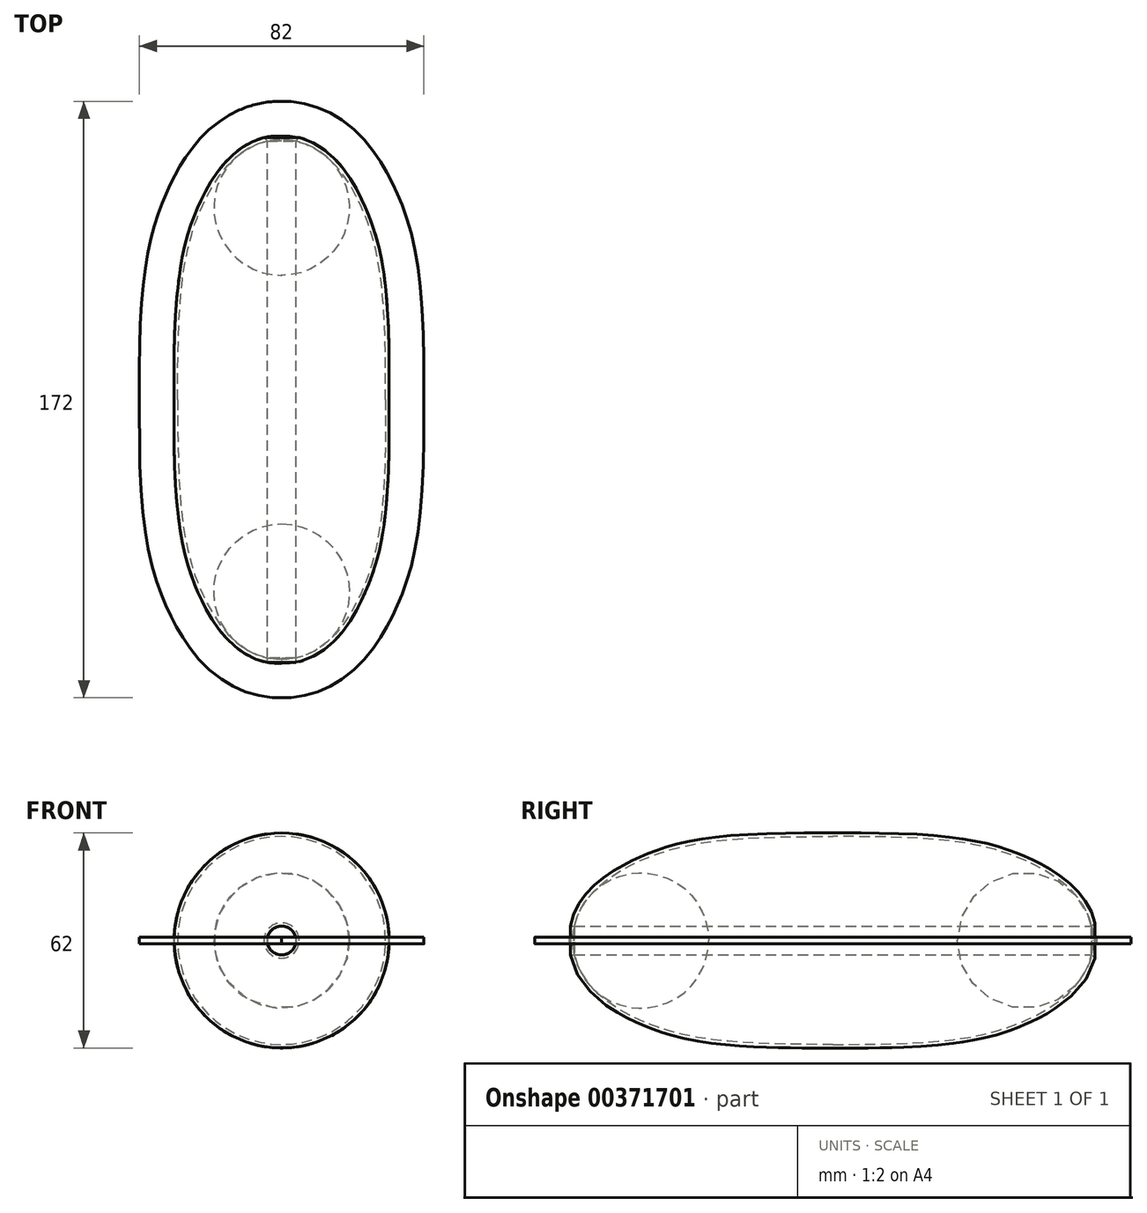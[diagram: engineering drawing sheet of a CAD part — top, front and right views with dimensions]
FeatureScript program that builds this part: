
annotation { "Feature Type Name" : "Feature", "Feature Type Description" : "" }
export const myFeature = defineFeature(function(context is Context, id is Id, definition is map)
    precondition{}
    {
        {
            var Q0;
            Q0=qCreatedBy(makeId("Top.planeOp"),FACE);
            var sketch = newSketch(context, id + "F0", { "sketchPlane" : qUnion([Q0])});
            skLineSegment(sketch, "E0", {"start": v(-51.66, 84.82) * mm, "end": v(-51.66, -137.93) * mm});
            skFitSpline(sketch, "E1", {"points": [v(-51.66, 75) * mm, v(-74.62, 55.7) * mm, v(-81.66, 0) * mm], "startDerivative": vector(-82.27, 0) * mm, "endDerivative": vector(0, -150.55) * mm});
            skFitSpline(sketch, "E2.MirrorCS", {"points": [v(-51.66, -75) * mm, v(-74.62, -55.7) * mm, v(-81.66, 0) * mm], "startDerivative": vector(-82.27, 0) * mm, "endDerivative": vector(0, 150.55) * mm});
            skFitSpline(sketch, "E3.MirrorCS", {"points": [v(-51.66, 75) * mm, v(-28.7, 55.7) * mm, v(-21.66, 0) * mm], "startDerivative": vector(82.27, 0) * mm, "endDerivative": vector(0, -150.55) * mm});
            skFitSpline(sketch, "E4.MirrorCS", {"points": [v(-51.66, -75) * mm, v(-28.7, -55.7) * mm, v(-21.66, 0) * mm], "startDerivative": vector(82.27, 0) * mm, "endDerivative": vector(0, 150.55) * mm});
            skLineSegment(sketch, "E5", {"start": v(-55.82, -80.1) * mm, "end": v(-55.82, 74.56) * mm});
            skLineSegment(sketch, "E6", {"start": v(-55.82, 74.56) * mm, "end": v(-64.04, 83.73) * mm});
            skFitSpline(sketch, "E7.0", {"points": [v(-51.66, 76) * mm, v(-53.46, 76) * mm, v(-56.85, 75.56) * mm, v(-61.36, 73.76) * mm, v(-65.28, 71.04) * mm, v(-68.66, 67.6) * mm, v(-71.55, 63.68) * mm, v(-73.59, 60.14) * mm, v(-75.03, 57.23) * mm, v(-76.01, 55.05) * mm, v(-76.91, 52.86) * mm, v(-78, 49.9) * mm, v(-79.17, 46.1) * mm, v(-80.29, 41.26) * mm, v(-81.15, 36.05) * mm, v(-82, 28.44) * mm, v(-82.56, 17.39) * mm, v(-82.66, 6.28) * mm, v(-82.66, 0) * mm]});
            skFitSpline(sketch, "E7.1", {"points": [v(-51.66, 76) * mm, v(-49.86, 76) * mm, v(-46.47, 75.56) * mm, v(-41.96, 73.76) * mm, v(-38.04, 71.04) * mm, v(-34.66, 67.6) * mm, v(-31.77, 63.68) * mm, v(-29.73, 60.14) * mm, v(-28.3, 57.23) * mm, v(-27.3, 55.05) * mm, v(-26.4, 52.86) * mm, v(-25.32, 49.9) * mm, v(-24.15, 46.1) * mm, v(-23.03, 41.26) * mm, v(-22.17, 36.05) * mm, v(-21.33, 28.44) * mm, v(-20.76, 17.39) * mm, v(-20.66, 6.28) * mm, v(-20.66, 0) * mm]});
            skFitSpline(sketch, "E7.2", {"points": [v(-51.66, -76) * mm, v(-49.86, -76) * mm, v(-46.47, -75.56) * mm, v(-41.96, -73.76) * mm, v(-38.04, -71.04) * mm, v(-34.66, -67.6) * mm, v(-31.77, -63.68) * mm, v(-29.73, -60.14) * mm, v(-28.3, -57.23) * mm, v(-27.3, -55.05) * mm, v(-26.4, -52.86) * mm, v(-25.32, -49.9) * mm, v(-24.15, -46.1) * mm, v(-23.03, -41.26) * mm, v(-22.17, -36.05) * mm, v(-21.33, -28.44) * mm, v(-20.76, -17.39) * mm, v(-20.66, -6.28) * mm, v(-20.66, 0) * mm]});
            skFitSpline(sketch, "E7.3", {"points": [v(-51.66, -76) * mm, v(-53.46, -76) * mm, v(-56.85, -75.56) * mm, v(-61.36, -73.76) * mm, v(-65.28, -71.04) * mm, v(-68.66, -67.6) * mm, v(-71.55, -63.68) * mm, v(-73.59, -60.14) * mm, v(-75.03, -57.23) * mm, v(-76.01, -55.05) * mm, v(-76.91, -52.86) * mm, v(-78, -49.9) * mm, v(-79.17, -46.1) * mm, v(-80.29, -41.26) * mm, v(-81.15, -36.05) * mm, v(-82, -28.44) * mm, v(-82.56, -17.39) * mm, v(-82.66, -6.28) * mm, v(-82.66, 0) * mm]});
            skFitSpline(sketch, "E8.0", {"points": [v(-51.66, 86) * mm, v(-52.97, 86) * mm, v(-55.55, 85.84) * mm, v(-59.28, 85.13) * mm, v(-62.79, 83.98) * mm, v(-66.04, 82.47) * mm, v(-69, 80.65) * mm, v(-72.57, 77.91) * mm, v(-75.6, 74.83) * mm, v(-78.16, 71.59) * mm, v(-79.88, 69.1) * mm, v(-81.43, 66.57) * mm, v(-82.82, 64.03) * mm, v(-84.07, 61.5) * mm, v(-85.2, 59) * mm, v(-86.23, 56.49) * mm, v(-87.5, 53.07) * mm, v(-88.84, 48.68) * mm, v(-90.1, 43.18) * mm, v(-91.06, 37.38) * mm, v(-91.97, 29.15) * mm, v(-92.56, 17.6) * mm, v(-92.66, 6.33) * mm, v(-92.66, 0) * mm]});
            skFitSpline(sketch, "E8.1", {"points": [v(-51.66, 86) * mm, v(-50.35, 86) * mm, v(-47.77, 85.84) * mm, v(-44.04, 85.13) * mm, v(-40.53, 83.98) * mm, v(-37.28, 82.47) * mm, v(-34.31, 80.65) * mm, v(-30.75, 77.91) * mm, v(-27.73, 74.83) * mm, v(-25.16, 71.59) * mm, v(-23.44, 69.1) * mm, v(-21.89, 66.57) * mm, v(-20.5, 64.03) * mm, v(-19.25, 61.5) * mm, v(-18.12, 59) * mm, v(-17.09, 56.49) * mm, v(-15.83, 53.07) * mm, v(-14.48, 48.68) * mm, v(-13.21, 43.18) * mm, v(-12.26, 37.38) * mm, v(-11.35, 29.15) * mm, v(-10.76, 17.6) * mm, v(-10.66, 6.33) * mm, v(-10.66, 0) * mm]});
            skFitSpline(sketch, "E8.2", {"points": [v(-51.66, -86) * mm, v(-50.35, -86) * mm, v(-47.77, -85.84) * mm, v(-44.04, -85.13) * mm, v(-40.53, -83.98) * mm, v(-37.28, -82.47) * mm, v(-34.31, -80.65) * mm, v(-30.75, -77.91) * mm, v(-27.73, -74.83) * mm, v(-25.16, -71.59) * mm, v(-23.44, -69.1) * mm, v(-21.89, -66.57) * mm, v(-20.5, -64.03) * mm, v(-19.25, -61.5) * mm, v(-18.12, -59) * mm, v(-17.09, -56.49) * mm, v(-15.83, -53.07) * mm, v(-14.48, -48.68) * mm, v(-13.21, -43.18) * mm, v(-12.26, -37.38) * mm, v(-11.35, -29.15) * mm, v(-10.76, -17.6) * mm, v(-10.66, -6.33) * mm, v(-10.66, 0) * mm]});
            skFitSpline(sketch, "E8.3", {"points": [v(-51.66, -86) * mm, v(-52.97, -86) * mm, v(-55.55, -85.84) * mm, v(-59.28, -85.13) * mm, v(-62.79, -83.98) * mm, v(-66.04, -82.47) * mm, v(-69, -80.65) * mm, v(-72.57, -77.91) * mm, v(-75.6, -74.83) * mm, v(-78.16, -71.59) * mm, v(-79.88, -69.1) * mm, v(-81.43, -66.57) * mm, v(-82.82, -64.03) * mm, v(-84.07, -61.5) * mm, v(-85.2, -59) * mm, v(-86.23, -56.49) * mm, v(-87.5, -53.07) * mm, v(-88.84, -48.68) * mm, v(-90.1, -43.18) * mm, v(-91.06, -37.38) * mm, v(-91.97, -29.15) * mm, v(-92.56, -17.6) * mm, v(-92.66, -6.33) * mm, v(-92.66, 0) * mm]});
            skSolve(sketch);
        }
        {
            var Q0;
            {var subQ2=sQuery(id+"F0.wireOp",EDGE,"E1");var subQ6=sQuery(id+"F0.wireOp",EDGE,"E2.MirrorCS");var subQ7=makeQuery(id+"F0.imprint","INTERSECT",VERTEX,{"derivedFrom":[subQ2,subQ6]});Q0=makeQuery(id+"F0.imprint","IMPRINT",FACE,{"disambiguationData":[TD([[makeQuery(id+"F0.imprint","IMPRINT",EDGE,{"disambiguationData":[TD([[subQ7,1.0]])],"derivedFrom":subQ6}),1.0]])]});}
            var Q1;
            {var subQ3=sQuery(id+"F0.wireOp",EDGE,"E2.MirrorCS");var subQ5=sQuery(id+"F0.wireOp",EDGE,"E5");var subQ6=makeQuery(id+"F0.imprint","INTERSECT",VERTEX,{"derivedFrom":[subQ3,subQ5]});Q1=makeQuery(id+"F0.imprint","IMPRINT",FACE,{"disambiguationData":[TD([[makeQuery(id+"F0.imprint","IMPRINT",EDGE,{"disambiguationData":[TD([[subQ6,1.0]])],"derivedFrom":subQ3}),-1.0]])]});}
            var Q2;
            Q2=sQuery(id+"F0.wireOp",EDGE,"E0");
            revolve(context, id + "F1", {"entities" : qUnion([Q0, Q1]), "axis" : qUnion([Q2]), "revolveType" : RevolveType.FULL});
        }
        {
            var Q0;
            {var subQ0=sQuery(id+"F0.wireOp",EDGE,"E7.1");Q0=makeQuery(id+"F0.imprint","IMPRINT",FACE,{"disambiguationData":[TD([[makeQuery(id+"F0.imprint","IMPRINT",EDGE,{"derivedFrom":subQ0}),1.0]])]});}
            var Q1;
            {var subQ10=sQuery(id+"F0.wireOp",EDGE,"E8.3");Q1=makeQuery(id+"F0.imprint","IMPRINT",FACE,{"disambiguationData":[TD([[makeQuery(id+"F0.imprint","IMPRINT",EDGE,{"derivedFrom":subQ10}),-1.0]])]});}
            extrude(context, id + "F2", {"entities" : qUnion([Q0, Q1]), "operationType" : NewBodyOperationType.ADD, "endBound" : BoundingType.SYMMETRIC, "depth" : 2 * mm});
        }
    });
